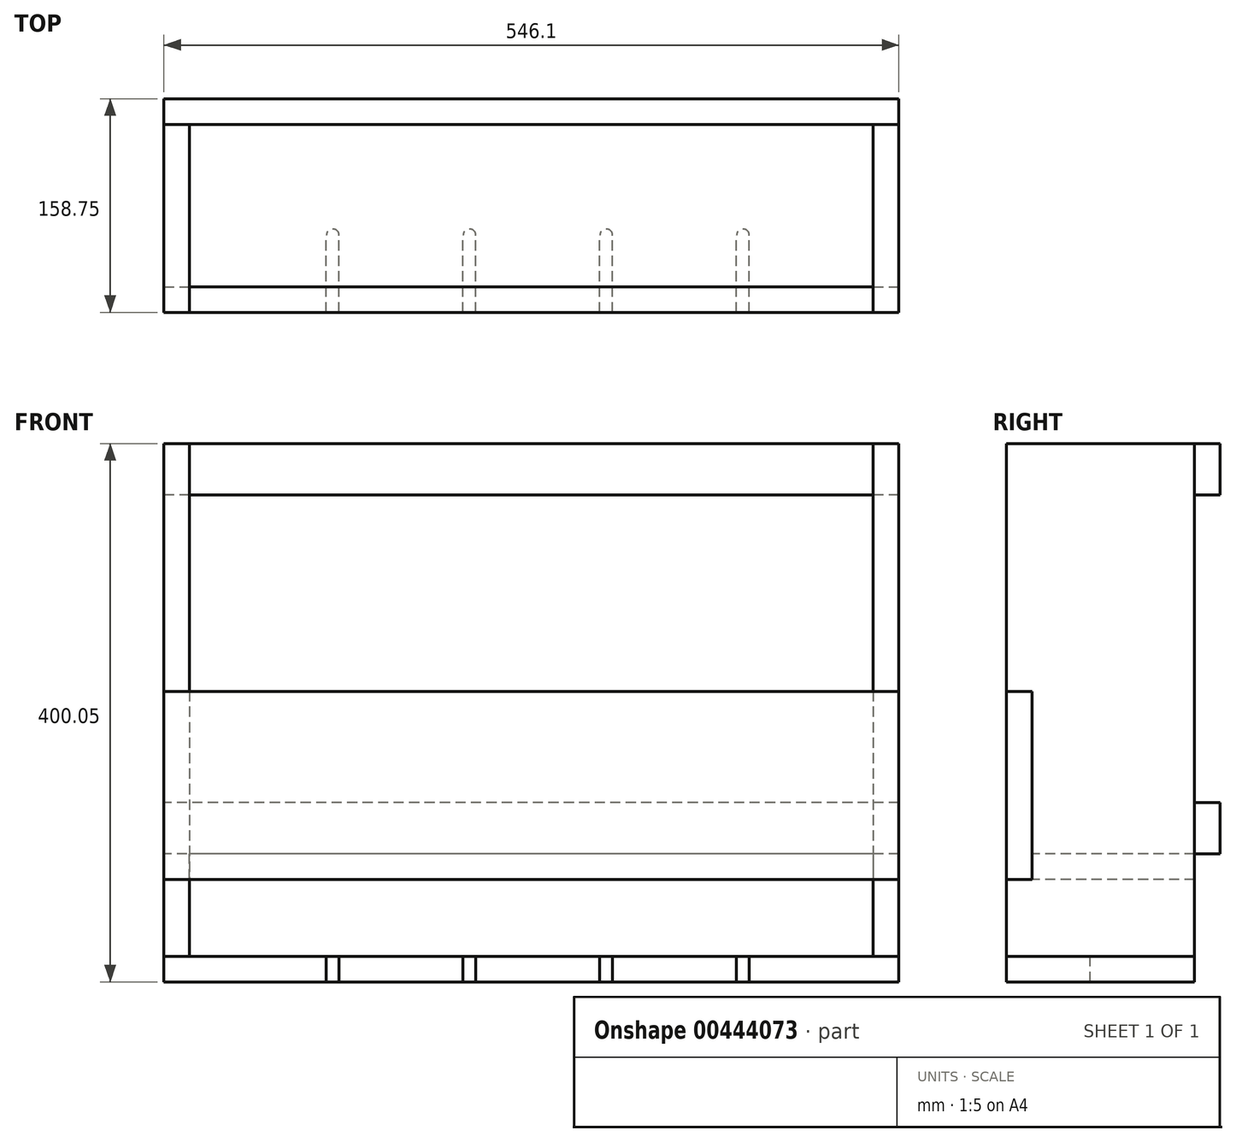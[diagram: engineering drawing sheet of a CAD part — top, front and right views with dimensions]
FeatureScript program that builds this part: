
annotation { "Feature Type Name" : "Feature", "Feature Type Description" : "" }
export const myFeature = defineFeature(function(context is Context, id is Id, definition is map)
    precondition{}
    {
        {
            var Q0;
            Q0=qCreatedBy(makeId("Top.planeOp"),FACE);
            var sketch = newSketch(context, id + "F0", { "sketchPlane" : qUnion([Q0])});
            skLineSegment(sketch, "E0.bottom", {"start": v(0, 0) * mm, "end": v(546.1, 0) * mm});
            skLineSegment(sketch, "E0.top", {"start": v(0, -139.7) * mm, "end": v(120.65, -139.7) * mm});
            skLineSegment(sketch, "E0.left", {"start": v(0, 0) * mm, "end": v(0, -139.7) * mm});
            skLineSegment(sketch, "E0.right", {"start": v(546.1, 0) * mm, "end": v(546.1, -139.7) * mm});
            skLineSegment(sketch, "E1.left", {"start": v(120.65, -139.7) * mm, "end": v(120.65, -82.55) * mm});
            skLineSegment(sketch, "E1.right", {"start": v(130.18, -139.7) * mm, "end": v(130.18, -82.55) * mm});
            skArc(sketch, "E2", {"start": v(130.18, -82.55) * mm, "mid": v(125.41, -77.79) * mm, "end": v(120.65, -82.55) * mm});
            skLineSegment(sketch, "E3.trimOffspring", {"start": v(130.18, -139.7) * mm, "end": v(222.25, -139.7) * mm});
            skLineSegment(sketch, "E4.1.0.0", {"start": v(222.25, -139.7) * mm, "end": v(222.25, -82.55) * mm});
            skLineSegment(sketch, "E4.1.0.1", {"start": v(231.78, -139.7) * mm, "end": v(231.78, -82.55) * mm});
            skArc(sketch, "E4.1.0.2", {"start": v(231.78, -82.55) * mm, "mid": v(227.01, -77.79) * mm, "end": v(222.25, -82.55) * mm});
            skLineSegment(sketch, "E4.2.0.0", {"start": v(323.85, -139.7) * mm, "end": v(323.85, -82.55) * mm});
            skLineSegment(sketch, "E4.2.0.1", {"start": v(333.38, -139.7) * mm, "end": v(333.38, -82.55) * mm});
            skArc(sketch, "E4.2.0.2", {"start": v(333.38, -82.55) * mm, "mid": v(328.61, -77.79) * mm, "end": v(323.85, -82.55) * mm});
            skLineSegment(sketch, "E4.3.0.0", {"start": v(425.45, -139.7) * mm, "end": v(425.45, -82.55) * mm});
            skLineSegment(sketch, "E4.3.0.1", {"start": v(434.98, -139.7) * mm, "end": v(434.98, -82.55) * mm});
            skArc(sketch, "E4.3.0.2", {"start": v(434.98, -82.55) * mm, "mid": v(430.21, -77.79) * mm, "end": v(425.45, -82.55) * mm});
            skLineSegment(sketch, "E4.direction1", {"start": v(120.65, -139.7) * mm, "end": v(222.25, -139.7) * mm, "construction": true});
            skLineSegment(sketch, "E5.trimOffspring", {"start": v(231.78, -139.7) * mm, "end": v(323.85, -139.7) * mm});
            skLineSegment(sketch, "E6.trimOffspring", {"start": v(333.38, -139.7) * mm, "end": v(425.45, -139.7) * mm});
            skLineSegment(sketch, "E7.trimOffspring", {"start": v(434.98, -139.7) * mm, "end": v(546.1, -139.7) * mm});
            skSolve(sketch);
        }
        {
            var Q0;
            Q0=makeQuery(id+"F0.imprint","IMPRINT",FACE,{"disambiguationData":[TD([[makeQuery(id+"F0.imprint","IMPRINT",EDGE,{"derivedFrom":sQuery(id+"F0.wireOp",EDGE,"E0.bottom")}),-1.0]])]});
            extrude(context, id + "F1", {"entities" : qUnion([Q0]), "depth" : 19.05 * mm});
        }
        {
            var Q0;
            Q0=makeQuery(id+"F1.opExtrude","CAP_FACE",FACE,{"disambiguationData":[OSD([sQuery(id+"F0.wireOp",EDGE,"E0.bottom"),sQuery(id+"F0.wireOp",EDGE,"E0.top"),sQuery(id+"F0.wireOp",EDGE,"E0.left"),sQuery(id+"F0.wireOp",EDGE,"E0.right"),sQuery(id+"F0.wireOp",EDGE,"E1.left"),sQuery(id+"F0.wireOp",EDGE,"E1.right"),sQuery(id+"F0.wireOp",EDGE,"E2"),sQuery(id+"F0.wireOp",EDGE,"E3.trimOffspring"),sQuery(id+"F0.wireOp",EDGE,"E4.1.0.0"),sQuery(id+"F0.wireOp",EDGE,"E4.1.0.1"),sQuery(id+"F0.wireOp",EDGE,"E4.1.0.2"),sQuery(id+"F0.wireOp",EDGE,"E4.2.0.0"),sQuery(id+"F0.wireOp",EDGE,"E4.2.0.1"),sQuery(id+"F0.wireOp",EDGE,"E4.2.0.2"),sQuery(id+"F0.wireOp",EDGE,"E4.3.0.0"),sQuery(id+"F0.wireOp",EDGE,"E4.3.0.1"),sQuery(id+"F0.wireOp",EDGE,"E4.3.0.2"),sQuery(id+"F0.wireOp",EDGE,"E5.trimOffspring"),sQuery(id+"F0.wireOp",EDGE,"E6.trimOffspring"),sQuery(id+"F0.wireOp",EDGE,"E7.trimOffspring")])],"isStart":false});
            var sketch = newSketch(context, id + "F2", { "sketchPlane" : qUnion([Q0])});
            skLineSegment(sketch, "E8.bottom", {"start": v(0, 0) * mm, "end": v(19.05, 0) * mm});
            skLineSegment(sketch, "E8.top", {"start": v(0, -139.7) * mm, "end": v(19.05, -139.7) * mm});
            skLineSegment(sketch, "E8.left", {"start": v(0, 0) * mm, "end": v(0, -139.7) * mm});
            skLineSegment(sketch, "E8.right", {"start": v(19.05, 0) * mm, "end": v(19.05, -139.7) * mm});
            skLineSegment(sketch, "E9.bottom", {"start": v(546.1, 0) * mm, "end": v(527.05, 0) * mm});
            skLineSegment(sketch, "E9.top", {"start": v(546.1, -139.7) * mm, "end": v(527.05, -139.7) * mm});
            skLineSegment(sketch, "E9.left", {"start": v(546.1, 0) * mm, "end": v(546.1, -139.7) * mm});
            skLineSegment(sketch, "E9.right", {"start": v(527.05, 0) * mm, "end": v(527.05, -139.7) * mm});
            skSolve(sketch);
        }
        {
            var Q0;
            Q0=makeQuery(id+"F2.imprint","IMPRINT",FACE,{"disambiguationData":[TD([[makeQuery(id+"F2.imprint","IMPRINT",EDGE,{"derivedFrom":sQuery(id+"F2.wireOp",EDGE,"E9.bottom")}),-1.0]])]});
            var Q1;
            Q1=makeQuery(id+"F2.imprint","IMPRINT",FACE,{"disambiguationData":[TD([[makeQuery(id+"F2.imprint","IMPRINT",EDGE,{"derivedFrom":sQuery(id+"F2.wireOp",EDGE,"E8.bottom")}),-1.0]])]});
            extrude(context, id + "F3", {"entities" : qUnion([Q0, Q1]), "depth" : 381 * mm});
        }
        {
            var Q0;
            Q0=makeQuery(id+"F3.opExtrude","SWEPT_FACE",FACE,{"disambiguationData":[OSD([sQuery(id+"F2.wireOp",EDGE,"E8.top")])]});
            var sketch = newSketch(context, id + "F4", { "sketchPlane" : qUnion([Q0])});
            skLineSegment(sketch, "E10.bottom", {"start": v(19.05, 76.2) * mm, "end": v(527.05, 76.2) * mm});
            skLineSegment(sketch, "E10.top", {"start": v(19.05, 95.25) * mm, "end": v(527.05, 95.25) * mm});
            skLineSegment(sketch, "E10.left", {"start": v(19.05, 76.2) * mm, "end": v(19.05, 95.25) * mm});
            skLineSegment(sketch, "E10.right", {"start": v(527.05, 76.2) * mm, "end": v(527.05, 95.25) * mm});
            skSolve(sketch);
        }
        {
            var Q0;
            Q0 = qSketchRegion(id + "F4", true);
            var Q1;
            Q1=makeQuery(id+"F3.opExtrude","SWEPT_FACE",FACE,{"disambiguationData":[OSD([sQuery(id+"F2.wireOp",EDGE,"E8.bottom")])]});
            extrude(context, id + "F5", {"entities" : qUnion([Q0]), "endBound" : BoundingType.UP_TO_SURFACE, "oppositeDirection" : true, "endBoundEntityFace" : qUnion([Q1]), "depth" : 25.4 * mm});
        }
        {
            var Q0;
            Q0=makeQuery(id+"F5.opExtrude","CAP_FACE",FACE,{"disambiguationData":[OSD([sQuery(id+"F4.wireOp",EDGE,"E10.bottom"),sQuery(id+"F4.wireOp",EDGE,"E10.top"),sQuery(id+"F4.wireOp",EDGE,"E10.left"),sQuery(id+"F4.wireOp",EDGE,"E10.right")])],"isStart":true});
            var sketch = newSketch(context, id + "F6", { "sketchPlane" : qUnion([Q0])});
            skLineSegment(sketch, "E11.bottom", {"start": v(0, 76.2) * mm, "end": v(546.1, 76.2) * mm});
            skLineSegment(sketch, "E11.top", {"start": v(0, 215.9) * mm, "end": v(546.1, 215.9) * mm});
            skLineSegment(sketch, "E11.left", {"start": v(0, 76.2) * mm, "end": v(0, 215.9) * mm});
            skLineSegment(sketch, "E11.right", {"start": v(546.1, 76.2) * mm, "end": v(546.1, 215.9) * mm});
            skSolve(sketch);
        }
        {
            var Q0;
            Q0 = qSketchRegion(id + "F6", true);
            extrude(context, id + "F7", {"entities" : qUnion([Q0]), "oppositeDirection" : true, "depth" : 19.05 * mm});
        }
        {
            var Q0;
            Q0=makeQuery(id+"F3.opExtrude","SWEPT_FACE",FACE,{"disambiguationData":[OSD([sQuery(id+"F2.wireOp",EDGE,"E9.bottom")])]});
            var sketch = newSketch(context, id + "F8", { "sketchPlane" : qUnion([Q0])});
            skLineSegment(sketch, "E12.bottom", {"start": v(-546.1, 95.25) * mm, "end": v(0, 95.25) * mm});
            skLineSegment(sketch, "E12.top", {"start": v(-546.1, 133.35) * mm, "end": v(0, 133.35) * mm});
            skLineSegment(sketch, "E12.left", {"start": v(-546.1, 95.25) * mm, "end": v(-546.1, 133.35) * mm});
            skLineSegment(sketch, "E12.right", {"start": v(0, 95.25) * mm, "end": v(0, 133.35) * mm});
            skLineSegment(sketch, "E13.bottom", {"start": v(-546.1, 400.05) * mm, "end": v(0, 400.05) * mm});
            skLineSegment(sketch, "E13.top", {"start": v(-546.1, 361.95) * mm, "end": v(0, 361.95) * mm});
            skLineSegment(sketch, "E13.left", {"start": v(-546.1, 400.05) * mm, "end": v(-546.1, 361.95) * mm});
            skLineSegment(sketch, "E13.right", {"start": v(0, 400.05) * mm, "end": v(0, 361.95) * mm});
            skSolve(sketch);
        }
        {
            var Q0;
            Q0 = qSketchRegion(id + "F8", true);
            extrude(context, id + "F9", {"entities" : qUnion([Q0]), "depth" : 19.05 * mm});
        }
        {
            var Q0;
            Q0=makeQuery(id+"F7.opExtrude","SWEPT_BODY",BODY,{"disambiguationData":[OSD([sQuery(id+"F6.wireOp",EDGE,"E11.bottom"),sQuery(id+"F6.wireOp",EDGE,"E11.top"),sQuery(id+"F6.wireOp",EDGE,"E11.left"),sQuery(id+"F6.wireOp",EDGE,"E11.right")])]});
            var Q1;
            Q1=makeQuery(id+"F3.opExtrude","SWEPT_BODY",BODY,{"disambiguationData":[OSD([sQuery(id+"F2.wireOp",EDGE,"E8.bottom"),sQuery(id+"F2.wireOp",EDGE,"E8.top"),sQuery(id+"F2.wireOp",EDGE,"E8.left"),sQuery(id+"F2.wireOp",EDGE,"E8.right")])]});
            var Q2;
            Q2=makeQuery(id+"F5.opExtrude","SWEPT_BODY",BODY,{"disambiguationData":[OSD([sQuery(id+"F4.wireOp",EDGE,"E10.bottom"),sQuery(id+"F4.wireOp",EDGE,"E10.top"),sQuery(id+"F4.wireOp",EDGE,"E10.left"),sQuery(id+"F4.wireOp",EDGE,"E10.right")])]});
            var Q3;
            Q3=makeQuery(id+"F3.opExtrude","SWEPT_BODY",BODY,{"disambiguationData":[OSD([sQuery(id+"F2.wireOp",EDGE,"E9.bottom"),sQuery(id+"F2.wireOp",EDGE,"E9.top"),sQuery(id+"F2.wireOp",EDGE,"E9.left"),sQuery(id+"F2.wireOp",EDGE,"E9.right")])]});
            booleanBodies(context, id + "F10", {"operationType" : BooleanOperationType.SUBTRACTION, "tools" : qUnion([Q0]), "targets" : qUnion([Q1, Q2, Q3]), "keepTools" : true});
        }
    });
